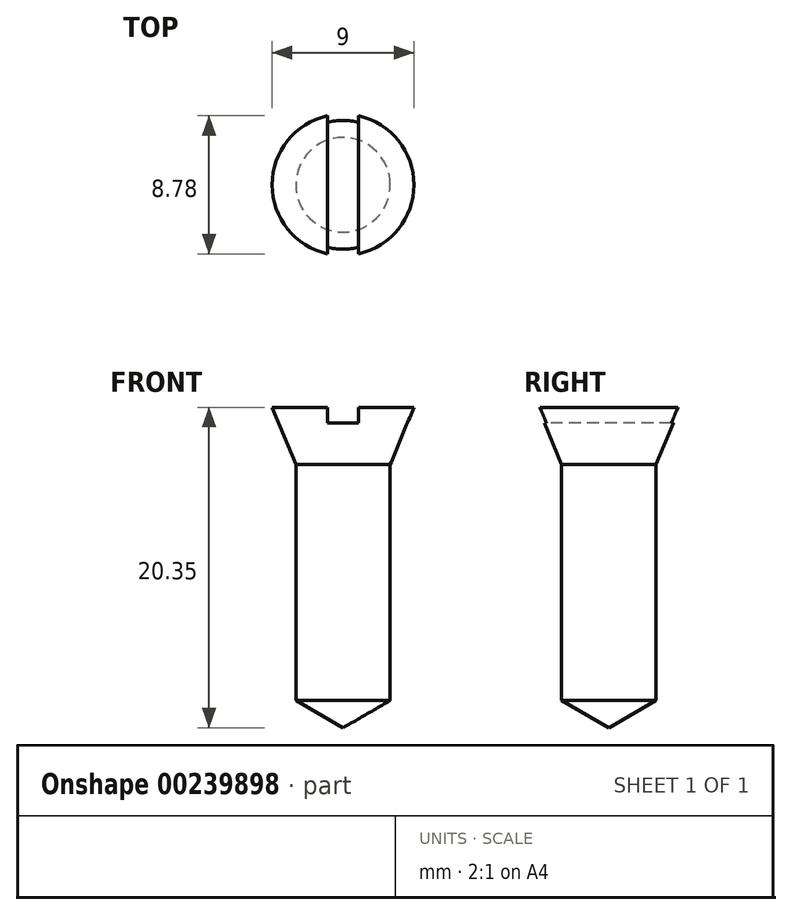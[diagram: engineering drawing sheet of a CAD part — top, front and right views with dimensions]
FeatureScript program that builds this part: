
annotation { "Feature Type Name" : "Feature", "Feature Type Description" : "" }
export const myFeature = defineFeature(function(context is Context, id is Id, definition is map)
    precondition{}
    {
        {
            var Q0;
            Q0=qCreatedBy(makeId("Front.planeOp"),FACE);
            var sketch = newSketch(context, id + "F0", { "sketchPlane" : qUnion([Q0])});
            skLineSegment(sketch, "E0", {"start": v(0, 0) * mm, "end": v(-3, 1.73) * mm});
            skLineSegment(sketch, "E1", {"start": v(-3, 1.73) * mm, "end": v(-3, 16.73) * mm});
            skLineSegment(sketch, "E2", {"start": v(-3, 16.73) * mm, "end": v(-4.5, 20.35) * mm});
            skLineSegment(sketch, "E3", {"start": v(-4.5, 20.35) * mm, "end": v(0, 20.35) * mm});
            skLineSegment(sketch, "E4", {"start": v(0, 20.35) * mm, "end": v(0, 0) * mm});
            skSolve(sketch);
        }
        {
            var Q0;
            Q0 = qSketchRegion(id + "F0", true);
            var Q1;
            Q1=sQuery(id+"F0.wireOp",EDGE,"E4");
            revolve(context, id + "F1", {"entities" : qUnion([Q0]), "axis" : qUnion([Q1]), "revolveType" : RevolveType.FULL});
        }
        {
            var Q0;
            Q0=qCreatedBy(makeId("Front.planeOp"),FACE);
            var sketch = newSketch(context, id + "F2", { "sketchPlane" : qUnion([Q0])});
            skLineSegment(sketch, "E5.0", {"start": v(-1, 20.35) * mm, "end": v(1, 20.35) * mm});
            skLineSegment(sketch, "E6", {"start": v(-1, 20.35) * mm, "end": v(-1, 19.35) * mm});
            skLineSegment(sketch, "E7", {"start": v(-1, 19.35) * mm, "end": v(1, 19.35) * mm});
            skLineSegment(sketch, "E8", {"start": v(1, 19.35) * mm, "end": v(1, 20.35) * mm});
            skPoint(sketch, "E9", {"position": v(0, 19.35) * mm});
            skSolve(sketch);
        }
        {
            var Q0;
            Q0 = qSketchRegion(id + "F2", true);
            extrude(context, id + "F3", {"entities" : qUnion([Q0]), "operationType" : NewBodyOperationType.REMOVE, "endBound" : BoundingType.SYMMETRIC, "oppositeDirection" : true, "depth" : 10 * mm});
        }
    });
